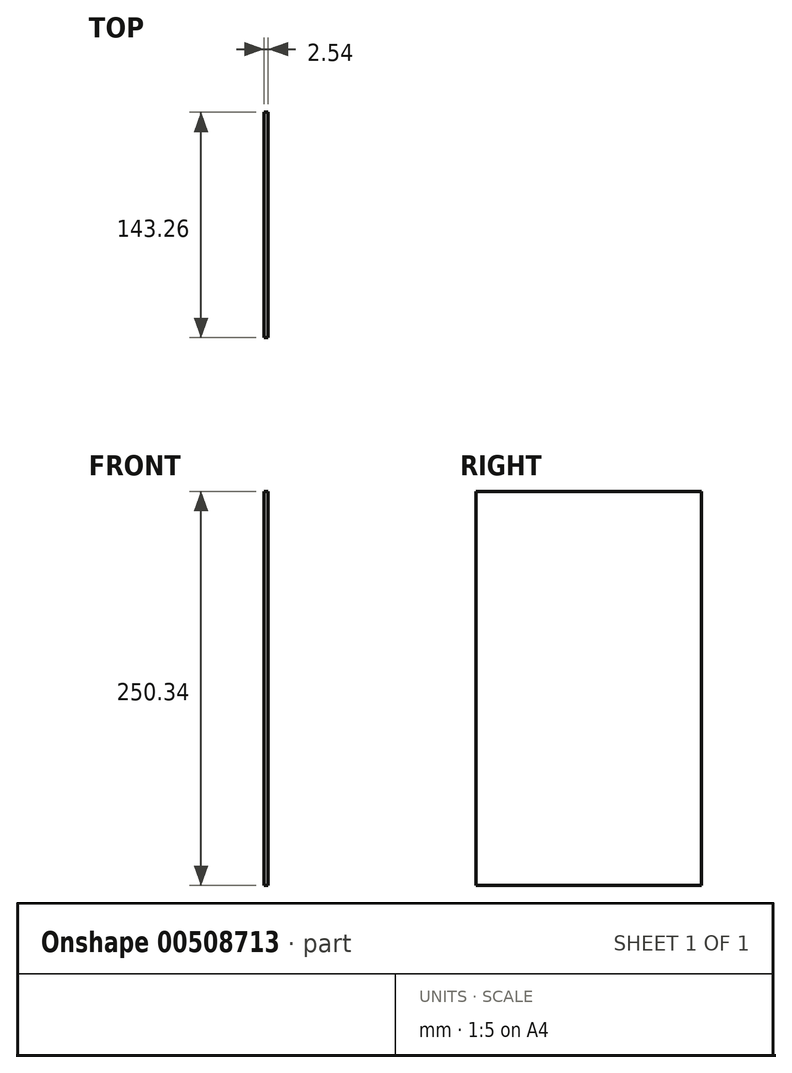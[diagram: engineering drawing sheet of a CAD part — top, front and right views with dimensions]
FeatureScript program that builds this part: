
annotation { "Feature Type Name" : "Feature", "Feature Type Description" : "" }
export const myFeature = defineFeature(function(context is Context, id is Id, definition is map)
    precondition{}
    {
        {
            var Q0;
            Q0=qCreatedBy(makeId("Front.planeOp"),FACE);
            var sketch = newSketch(context, id + "F0", { "sketchPlane" : qUnion([Q0])});
            skLineSegment(sketch, "E0", {"start": v(-34.48, 109.78) * mm, "end": v(-34.48, -140.56) * mm});
            skLineSegment(sketch, "E1", {"start": v(-34.48, -140.56) * mm, "end": v(-31.94, -140.56) * mm});
            skLineSegment(sketch, "E2", {"start": v(-31.94, -140.56) * mm, "end": v(-31.94, 109.78) * mm});
            skLineSegment(sketch, "E3", {"start": v(-31.94, 109.78) * mm, "end": v(-34.48, 109.78) * mm});
            skSolve(sketch);
        }
        {
            var Q0;
            Q0=makeQuery(id+"F0.imprint","IMPRINT",FACE,{"disambiguationData":[TD([[makeQuery(id+"F0.imprint","IMPRINT",EDGE,{"derivedFrom":sQuery(id+"F0.wireOp",EDGE,"E0")}),1.0]])]});
            extrude(context, id + "F1", {"entities" : qUnion([Q0]), "depth" : 143.26 * mm, "offsetDistance" : 25.4 * mm});
        }
    });
